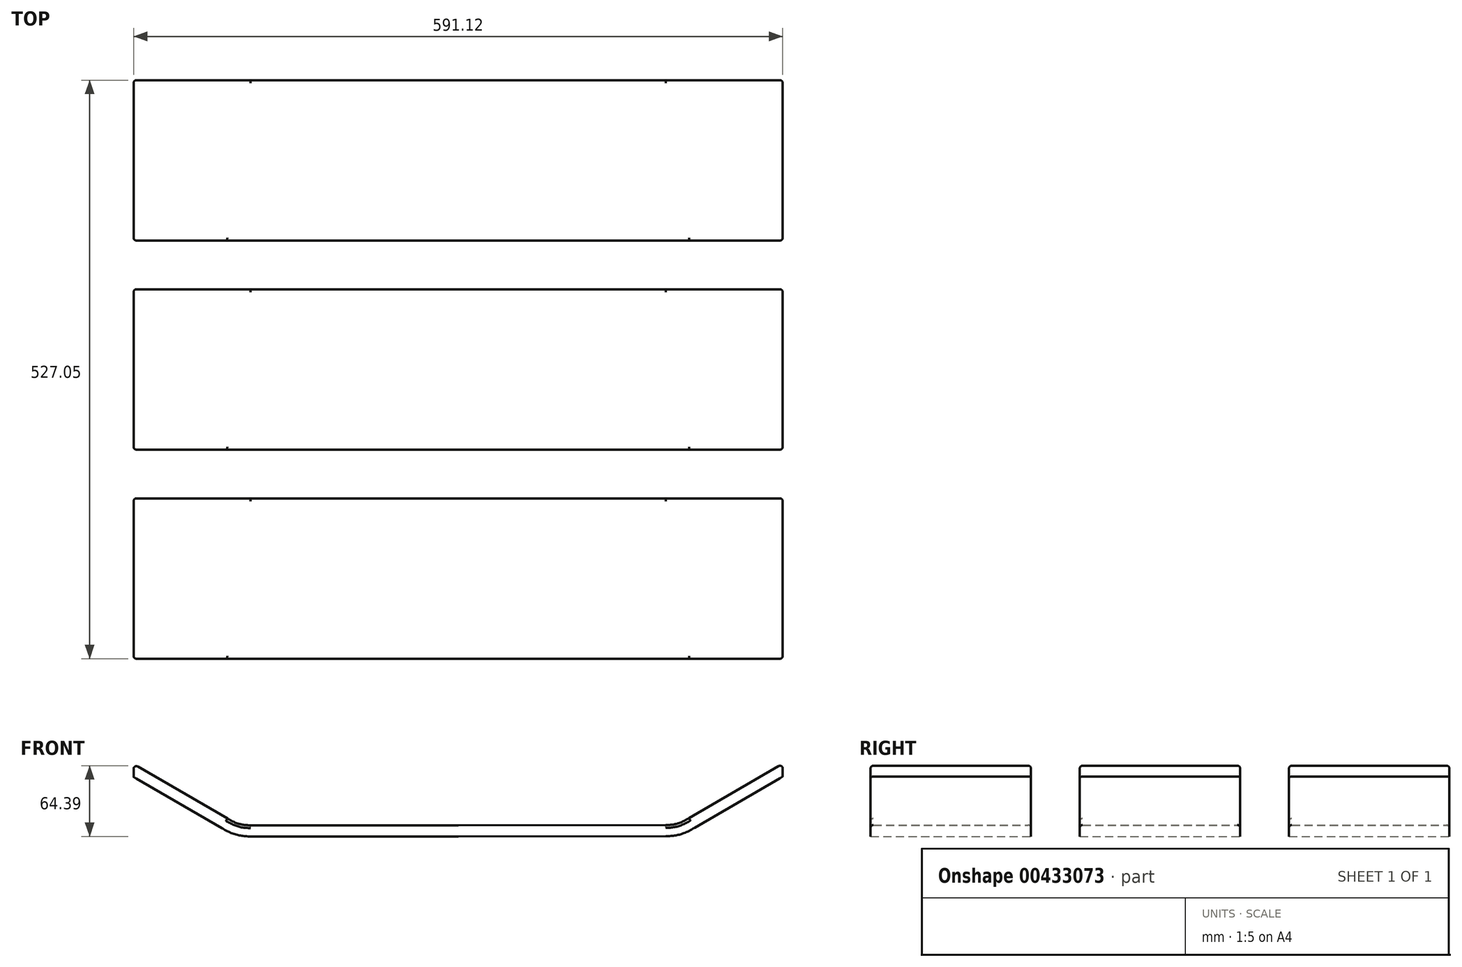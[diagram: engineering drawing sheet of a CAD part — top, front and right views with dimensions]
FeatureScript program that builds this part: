
annotation { "Feature Type Name" : "Feature", "Feature Type Description" : "" }
export const myFeature = defineFeature(function(context is Context, id is Id, definition is map)
    precondition{}
    {
        {
            var Q0;
            Q0=qCreatedBy(makeId("Front.planeOp"),FACE);
            var sketch = newSketch(context, id + "F0", { "sketchPlane" : qUnion([Q0])});
            skLineSegment(sketch, "E0", {"start": v(1.6, 54.16) * mm, "end": v(81.9, 7.54) * mm});
            skFitSpline(sketch, "E1", {"points": [v(81.9, 7.54) * mm, v(108.17, 0) * mm], "startDerivative": vector(31.2, -18.1) * mm, "endDerivative": vector(28.65, 0) * mm});
            skLineSegment(sketch, "E2", {"start": v(108.17, 0) * mm, "end": v(297.19, 0) * mm});
            skLineSegment(sketch, "E3.0", {"start": v(108.17, 10.16) * mm, "end": v(297.18, 10.16) * mm});
            skFitSpline(sketch, "E3.1", {"points": [v(87, 16.33) * mm, v(88.19, 15.64) * mm, v(90.4, 14.42) * mm, v(93.27, 13.02) * mm, v(95.8, 12) * mm, v(98.09, 11.26) * mm, v(100.3, 10.75) * mm, v(102.6, 10.4) * mm, v(105.15, 10.2) * mm, v(107.11, 10.16) * mm, v(108.17, 10.16) * mm]});
            skLineSegment(sketch, "E3.2", {"start": v(6.7, 62.94) * mm, "end": v(87, 16.33) * mm});
            skLineSegment(sketch, "E4", {"start": v(6.7, 62.94) * mm, "end": v(1.6, 65.9) * mm});
            skLineSegment(sketch, "E5", {"start": v(1.6, 65.9) * mm, "end": v(1.6, 54.16) * mm});
            skLineSegment(sketch, "E6", {"start": v(297.19, 0) * mm, "end": v(138.44, 0) * mm});
            skLineSegment(sketch, "E7.bottom", {"start": v(138.44, 0) * mm, "end": v(113.04, 0) * mm});
            skLineSegment(sketch, "E8", {"start": v(297.18, 10.16) * mm, "end": v(297.19, 0) * mm});
            skSolve(sketch);
        }
        {
            var Q0;
            Q0=makeQuery(id+"F0.imprint","IMPRINT",FACE,{"disambiguationData":[TD([[makeQuery(id+"F0.imprint","IMPRINT",EDGE,{"derivedFrom":sQuery(id+"F0.wireOp",EDGE,"E7.bottom")}),1.0]])]});
            var Q1;
            Q1=makeQuery(id+"F0.imprint","IMPRINT",FACE,{"disambiguationData":[TD([[makeQuery(id+"F0.imprint","IMPRINT",EDGE,{"derivedFrom":sQuery(id+"F0.wireOp",EDGE,"E0")}),1.0]])]});
            extrude(context, id + "F1", {"entities" : qUnion([Q0, Q1]), "depth" : 146.05 * mm});
        }
        {
            var Q0;
            Q0=makeQuery(id+"F1.opExtrude","CAP_EDGE",EDGE,{"disambiguationData":[OSD([sQuery(id+"F0.wireOp",EDGE,"E3.0")])],"isStart":true});
            var Q1;
            Q1=makeQuery(id+"F1.opExtrude","CAP_EDGE",EDGE,{"disambiguationData":[OSD([sQuery(id+"F0.wireOp",EDGE,"E3.1")])],"isStart":true});
            var Q2;
            Q2=makeQuery(id+"F1.opExtrude","CAP_EDGE",EDGE,{"disambiguationData":[OSD([sQuery(id+"F0.wireOp",EDGE,"E3.2"),sQuery(id+"F0.wireOp",EDGE,"E4")])],"isStart":true});
            var Q3;
            Q3=makeQuery(id+"F1.opExtrude","SWEPT_EDGE",EDGE,{"disambiguationData":[OSD([sQuery(id+"F0.wireOp",EDGE,"E4"),sQuery(id+"F0.wireOp",EDGE,"E5")])]});
            var Q4;
            Q4=makeQuery(id+"F1.opExtrude","CAP_EDGE",EDGE,{"disambiguationData":[OSD([sQuery(id+"F0.wireOp",EDGE,"E3.2"),sQuery(id+"F0.wireOp",EDGE,"E4")])],"isStart":false});
            var Q5;
            Q5=makeQuery(id+"F1.opExtrude","CAP_EDGE",EDGE,{"disambiguationData":[OSD([sQuery(id+"F0.wireOp",EDGE,"E3.1")])],"isStart":false});
            var Q6;
            Q6=makeQuery(id+"F1.opExtrude","CAP_EDGE",EDGE,{"disambiguationData":[OSD([sQuery(id+"F0.wireOp",EDGE,"E3.0")])],"isStart":false});
            var Q7;
            Q7=makeQuery(id+"F1.opExtrude","CAP_EDGE",EDGE,{"disambiguationData":[OSD([sQuery(id+"F0.wireOp",EDGE,"E5")])],"isStart":false});
            var Q8;
            Q8=makeQuery(id+"F1.opExtrude","CAP_EDGE",EDGE,{"disambiguationData":[OSD([sQuery(id+"F0.wireOp",EDGE,"E5")])],"isStart":true});
            fillet(context, id + "F2", {"entities" : qUnion([Q0, Q1, Q2, Q3, Q4, Q5, Q6, Q7, Q8]), "radius" : 2.54 * mm, "tangentPropagation" : true, "allowEdgeOverflow" : false});
        }
        {
            var Q0;
            Q0=makeQuery(id+"F1.opExtrude","SWEPT_BODY",BODY,{"disambiguationData":[OSD([sQuery(id+"F0.wireOp",EDGE,"E0"),sQuery(id+"F0.wireOp",EDGE,"E1"),sQuery(id+"F0.wireOp",EDGE,"E2"),sQuery(id+"F0.wireOp",EDGE,"E3.0"),sQuery(id+"F0.wireOp",EDGE,"E3.1"),sQuery(id+"F0.wireOp",EDGE,"E3.2"),sQuery(id+"F0.wireOp",EDGE,"E4"),sQuery(id+"F0.wireOp",EDGE,"E5"),sQuery(id+"F0.wireOp",EDGE,"E6"),sQuery(id+"F0.wireOp",EDGE,"E7.bottom"),sQuery(id+"F0.wireOp",EDGE,"E8")])]});
            var Q1;
            Q1=makeQuery(id+"F1.opExtrude","SWEPT_FACE",FACE,{"disambiguationData":[OSD([sQuery(id+"F0.wireOp",EDGE,"E8")])]});
            mirror(context, id + "F3", {"operationType" : NewBodyOperationType.ADD, "entities" : qUnion([Q0]), "mirrorPlane" : qUnion([Q1])});
        }
        {
            var Q0;
            Q0=makeQuery(id+"F1.opExtrude","SWEPT_BODY",BODY,{"disambiguationData":[OSD([sQuery(id+"F0.wireOp",EDGE,"E0"),sQuery(id+"F0.wireOp",EDGE,"E1"),sQuery(id+"F0.wireOp",EDGE,"E2"),sQuery(id+"F0.wireOp",EDGE,"E3.0"),sQuery(id+"F0.wireOp",EDGE,"E3.1"),sQuery(id+"F0.wireOp",EDGE,"E3.2"),sQuery(id+"F0.wireOp",EDGE,"E4"),sQuery(id+"F0.wireOp",EDGE,"E5"),sQuery(id+"F0.wireOp",EDGE,"E6"),sQuery(id+"F0.wireOp",EDGE,"E7.bottom"),sQuery(id+"F0.wireOp",EDGE,"E8")])]});
            transform(context, id + "F4", {"entities" : qUnion([Q0]), "transformType" : TransformType.TRANSLATION_3D, "dx" : 0 * mm, "dy" : 190.5 * mm, "dz" : 0 * mm, "makeCopy" : true});
        }
        {
            var Q0;
            Q0=makeQuery(id+"F4.opPattern","COPY",BODY,{"derivedFrom":makeQuery(id+"F1.opExtrude","SWEPT_BODY",BODY,{"disambiguationData":[OSD([sQuery(id+"F0.wireOp",EDGE,"E0"),sQuery(id+"F0.wireOp",EDGE,"E1"),sQuery(id+"F0.wireOp",EDGE,"E2"),sQuery(id+"F0.wireOp",EDGE,"E3.0"),sQuery(id+"F0.wireOp",EDGE,"E3.1"),sQuery(id+"F0.wireOp",EDGE,"E3.2"),sQuery(id+"F0.wireOp",EDGE,"E4"),sQuery(id+"F0.wireOp",EDGE,"E5"),sQuery(id+"F0.wireOp",EDGE,"E6"),sQuery(id+"F0.wireOp",EDGE,"E7.bottom"),sQuery(id+"F0.wireOp",EDGE,"E8")])]}),"instanceName":"1"});
            transform(context, id + "F5", {"entities" : qUnion([Q0]), "transformType" : TransformType.TRANSLATION_3D, "dx" : 0 * mm, "dy" : 190.5 * mm, "dz" : 0 * mm, "makeCopy" : true});
        }
    });
